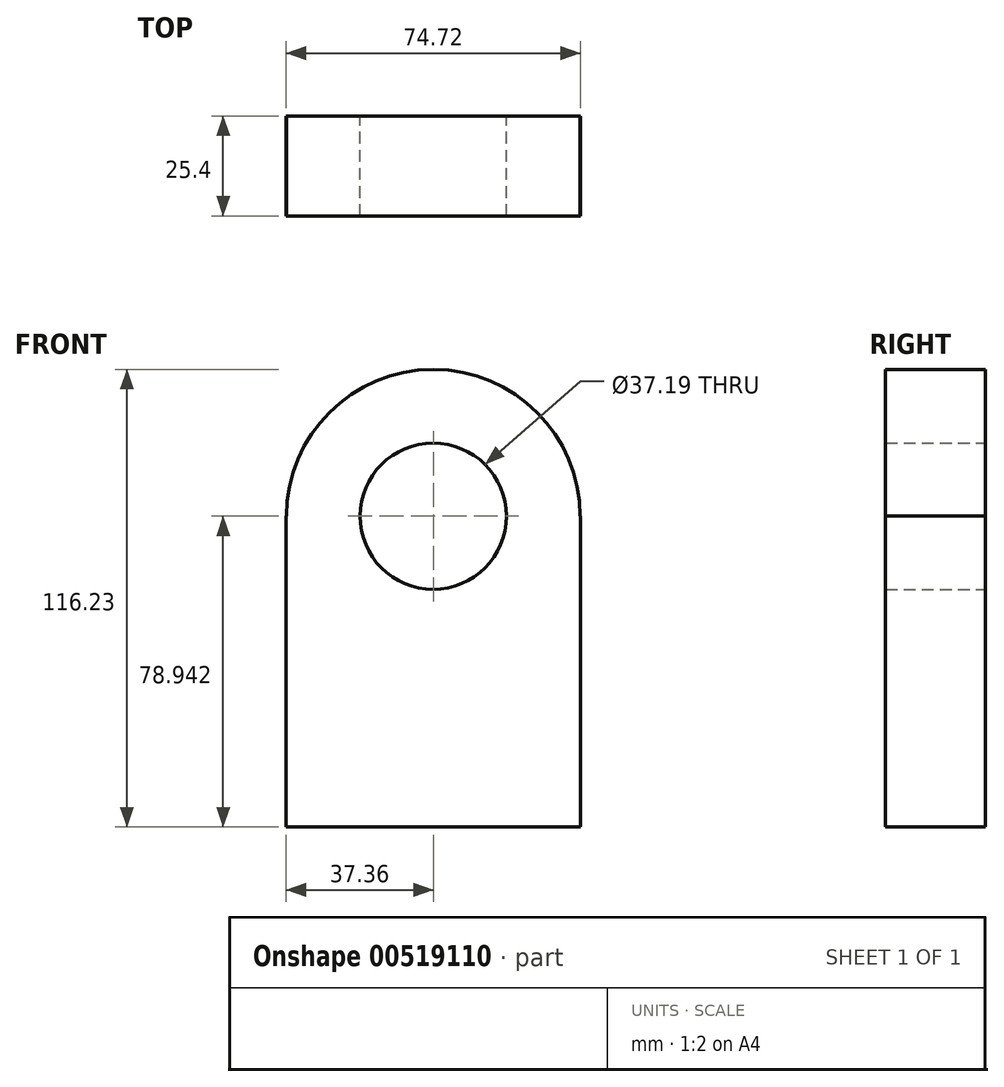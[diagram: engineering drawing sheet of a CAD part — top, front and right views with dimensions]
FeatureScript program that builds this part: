
annotation { "Feature Type Name" : "Feature", "Feature Type Description" : "" }
export const myFeature = defineFeature(function(context is Context, id is Id, definition is map)
    precondition{}
    {
        {
            var Q0;
            Q0=qCreatedBy(makeId("Front.planeOp"),FACE);
            var sketch = newSketch(context, id + "F0", { "sketchPlane" : qUnion([Q0])});
            skLineSegment(sketch, "E0.bottom", {"start": v(-37.36, 39.47) * mm, "end": v(37.36, 39.47) * mm});
            skLineSegment(sketch, "E0.top", {"start": v(-37.36, -39.47) * mm, "end": v(37.36, -39.47) * mm});
            skLineSegment(sketch, "E0.left", {"start": v(-37.36, 39.47) * mm, "end": v(-37.36, -39.47) * mm});
            skLineSegment(sketch, "E0.right", {"start": v(37.36, 39.47) * mm, "end": v(37.36, -39.47) * mm});
            skPoint(sketch, "E0.middle", {"position": v(0, 0) * mm});
            skCircle(sketch, "E1", {"center": v(0, 39.47) * mm, "radius": 37.3 * mm});
            skCircle(sketch, "E2", {"center": v(0, 39.47) * mm, "radius": 18.6 * mm});
            skSolve(sketch);
        }
        {
            var Q0;
            Q0=makeQuery(id+"F0.imprint","IMPRINT",FACE,{"disambiguationData":[TD([[makeQuery(id+"F0.imprint","IMPRINT",EDGE,{"derivedFrom":sQuery(id+"F0.wireOp",EDGE,"E0.top")}),1.0]])]});
            var Q1;
            {var subQ0=sQuery(id+"F0.wireOp",EDGE,"E1");var subQ1=sQuery(id+"F0.wireOp",EDGE,"E0.bottom");var subQ2=makeQuery(id+"F0.imprint","INTERSECT",VERTEX,{"disambiguationData":[OD(0.0)],"derivedFrom":[subQ1,subQ0]});Q1=makeQuery(id+"F0.imprint","IMPRINT",FACE,{"disambiguationData":[TD([[makeQuery(id+"F0.imprint","IMPRINT",EDGE,{"disambiguationData":[TD([[subQ2,-1.0]])],"derivedFrom":subQ1}),-1.0]])]});}
            var Q2;
            {var subQ0=sQuery(id+"F0.wireOp",EDGE,"E1");var subQ1=sQuery(id+"F0.wireOp",EDGE,"E0.bottom");var subQ2=makeQuery(id+"F0.imprint","INTERSECT",VERTEX,{"disambiguationData":[OD(0.0)],"derivedFrom":[subQ1,subQ0]});Q2=makeQuery(id+"F0.imprint","IMPRINT",FACE,{"disambiguationData":[TD([[makeQuery(id+"F0.imprint","IMPRINT",EDGE,{"disambiguationData":[TD([[subQ2,-1.0]])],"derivedFrom":subQ1}),1.0]])]});}
            extrude(context, id + "F1", {"entities" : qUnion([Q0, Q1, Q2]), "depth" : 25.4 * mm});
        }
    });
